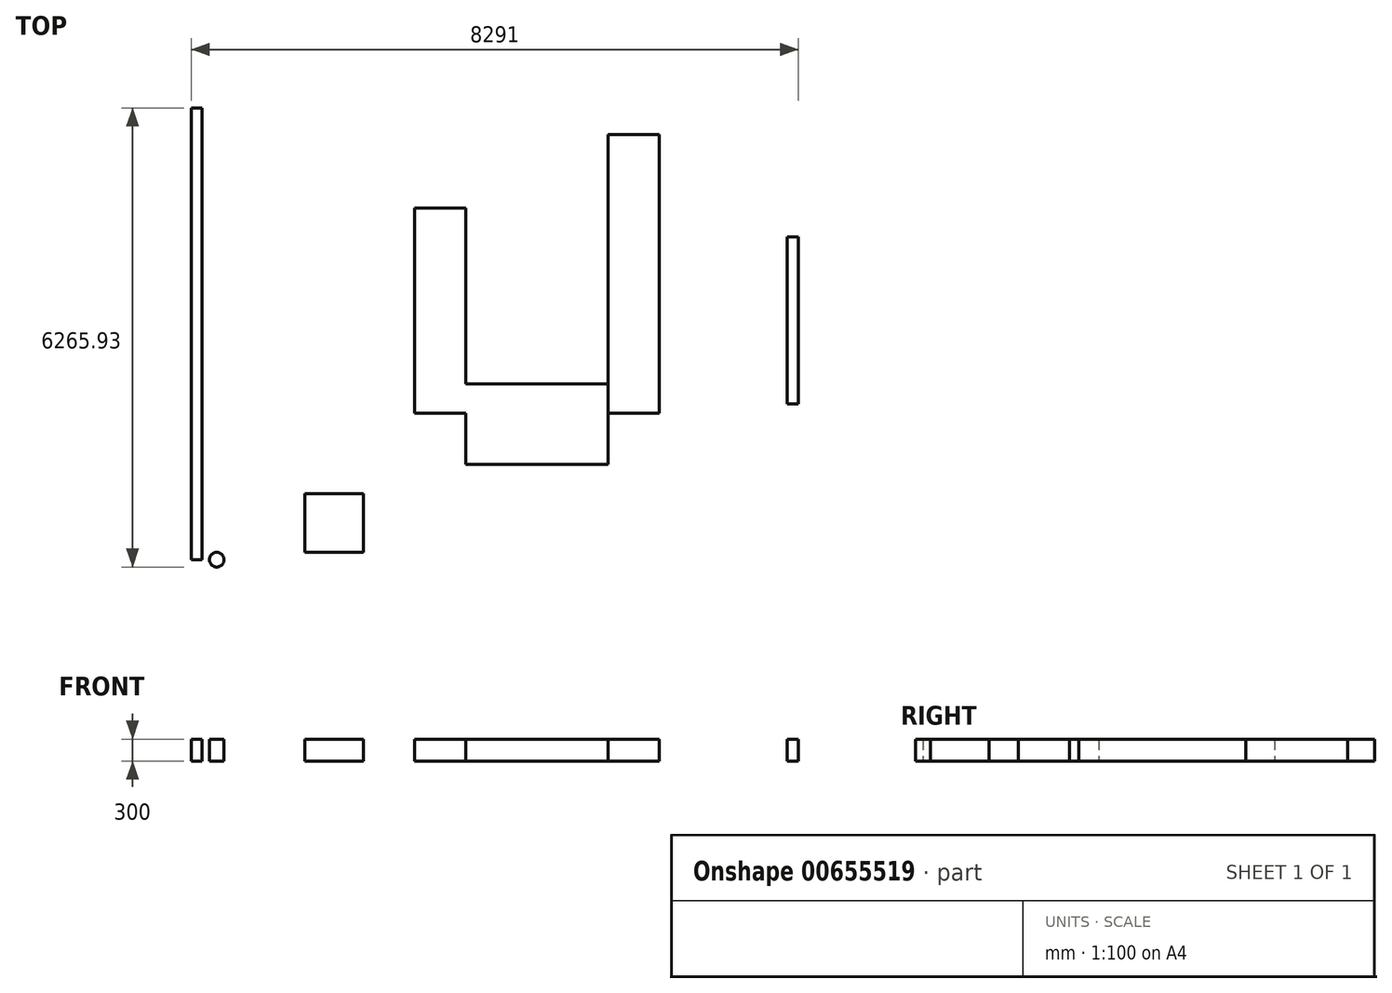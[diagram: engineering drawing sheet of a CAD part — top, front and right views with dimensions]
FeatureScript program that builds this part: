
annotation { "Feature Type Name" : "Feature", "Feature Type Description" : "" }
export const myFeature = defineFeature(function(context is Context, id is Id, definition is map)
    precondition{}
    {
        {
            var Q0;
            Q0=qCreatedBy(makeId("Top.planeOp"),FACE);
            var sketch = newSketch(context, id + "F0", { "sketchPlane" : qUnion([Q0])});
            skLineSegment(sketch, "E0.top", {"start": v(0, 700) * mm, "end": v(-300, 700) * mm, "construction": true});
            skLineSegment(sketch, "E0.left", {"start": v(0, 0) * mm, "end": v(0, 700) * mm, "construction": true});
            skLineSegment(sketch, "E1.bottom", {"start": v(800, -950) * mm, "end": v(2740, -950) * mm});
            skLineSegment(sketch, "E1.top", {"start": v(800, -1350) * mm, "end": v(2740, -1350) * mm});
            skLineSegment(sketch, "E1.left", {"start": v(800, -950) * mm, "end": v(800, -1350) * mm});
            skLineSegment(sketch, "E1.right", {"start": v(2740, -950) * mm, "end": v(2740, -1350) * mm});
            skLineSegment(sketch, "E2", {"start": v(5191, 1057.48) * mm, "end": v(5191, -1222.08) * mm});
            skLineSegment(sketch, "E3.bottom", {"start": v(800, -950) * mm, "end": v(100, -950) * mm});
            skLineSegment(sketch, "E3.top", {"start": v(800, 1450) * mm, "end": v(100, 1450) * mm});
            skLineSegment(sketch, "E3.left", {"start": v(800, -950) * mm, "end": v(800, 1450) * mm});
            skLineSegment(sketch, "E3.right", {"start": v(100, -950) * mm, "end": v(100, 1450) * mm});
            skLineSegment(sketch, "E4", {"start": v(-1400, -3250) * mm, "end": v(-1400, -2450) * mm});
            skLineSegment(sketch, "E5", {"start": v(-1400, -2450) * mm, "end": v(-600, -2450) * mm});
            skLineSegment(sketch, "E6", {"start": v(-600, -2450) * mm, "end": v(-600, -3250) * mm});
            skLineSegment(sketch, "E7", {"start": v(-600, -3250) * mm, "end": v(-1400, -3250) * mm});
            skCircle(sketch, "E8", {"center": v(-2600, -3350) * mm, "radius": 100 * mm});
            skLineSegment(sketch, "E9", {"start": v(5191, 1057.48) * mm, "end": v(5341, 1057.48) * mm});
            skLineSegment(sketch, "E10", {"start": v(5341, 1057.48) * mm, "end": v(5341, -1222.08) * mm});
            skLineSegment(sketch, "E11", {"start": v(5341, -1222.08) * mm, "end": v(5191, -1222.08) * mm});
            skLineSegment(sketch, "E12", {"start": v(100, -950) * mm, "end": v(100, -1350) * mm});
            skLineSegment(sketch, "E13", {"start": v(100, -1350) * mm, "end": v(800, -1350) * mm});
            skLineSegment(sketch, "E14", {"start": v(-2800, -3350) * mm, "end": v(-2800, 2815.93) * mm});
            skLineSegment(sketch, "E15", {"start": v(-2800, 2815.93) * mm, "end": v(-2950, 2815.93) * mm});
            skLineSegment(sketch, "E16", {"start": v(-2950, 2815.93) * mm, "end": v(-2950, -3350) * mm});
            skLineSegment(sketch, "E17", {"start": v(-2950, -3350) * mm, "end": v(-2800, -3350) * mm});
            skLineSegment(sketch, "E18", {"start": v(800, -1350) * mm, "end": v(800, -2050) * mm});
            skLineSegment(sketch, "E19", {"start": v(800, -2050) * mm, "end": v(2740, -2050) * mm});
            skLineSegment(sketch, "E20", {"start": v(2740, -2050) * mm, "end": v(2740, -1350) * mm});
            skLineSegment(sketch, "E21", {"start": v(800, -2050) * mm, "end": v(-600, -2450) * mm, "construction": true});
            skLineSegment(sketch, "E22", {"start": v(800, -1500) * mm, "end": v(2740, -1500) * mm, "construction": true});
            skLineSegment(sketch, "E23", {"start": v(-550, 700) * mm, "end": v(-550, 0) * mm, "construction": true});
            skLineSegment(sketch, "E24", {"start": v(-550, 700) * mm, "end": v(-300, 700) * mm, "construction": true});
            skLineSegment(sketch, "E25", {"start": v(-150, 700) * mm, "end": v(-150, 0) * mm, "construction": true});
            skLineSegment(sketch, "E26", {"start": v(-550, 700) * mm, "end": v(-700, 700) * mm, "construction": true});
            skLineSegment(sketch, "E27", {"start": v(-700, 700) * mm, "end": v(-700, 0) * mm, "construction": true});
            skLineSegment(sketch, "E28", {"start": v(800, -800) * mm, "end": v(2740, -800) * mm, "construction": true});
            skArc(sketch, "E29", {"start": v(0, 0) * mm, "mid": v(234.31, -565.69) * mm, "end": v(800, -800) * mm, "construction": true});
            skArc(sketch, "E30", {"start": v(-150, 0) * mm, "mid": v(128.25, -671.75) * mm, "end": v(800, -950) * mm, "construction": true});
            skArc(sketch, "E31", {"start": v(-550, 0) * mm, "mid": v(-154.6, -954.6) * mm, "end": v(800, -1350) * mm, "construction": true});
            skArc(sketch, "E32", {"start": v(-700, 0) * mm, "mid": v(-260.66, -1060.66) * mm, "end": v(800, -1500) * mm, "construction": true});
            skLineSegment(sketch, "E33", {"start": v(-700, 0) * mm, "end": v(-550, 0) * mm, "construction": true});
            skLineSegment(sketch, "E34", {"start": v(-550, 0) * mm, "end": v(-150, 0) * mm, "construction": true});
            skLineSegment(sketch, "E35", {"start": v(-150, 0) * mm, "end": v(0, 0) * mm, "construction": true});
            skLineSegment(sketch, "E36", {"start": v(-700, 700) * mm, "end": v(-700, 3100) * mm, "construction": true});
            skLineSegment(sketch, "E37", {"start": v(-700, 3100) * mm, "end": v(0, 3100) * mm, "construction": true});
            skLineSegment(sketch, "E38", {"start": v(0, 3100) * mm, "end": v(0, 700) * mm, "construction": true});
            skLineSegment(sketch, "E39.bottom", {"start": v(2741, -1349) * mm, "end": v(3441, -1349) * mm});
            skLineSegment(sketch, "E39.top", {"start": v(2741, 2451) * mm, "end": v(3441, 2451) * mm});
            skLineSegment(sketch, "E39.left", {"start": v(2741, -1349) * mm, "end": v(2741, 2451) * mm});
            skLineSegment(sketch, "E39.right", {"start": v(3441, -1349) * mm, "end": v(3441, 2451) * mm});
            skSolve(sketch);
        }
        {
            var Q0;
            Q0=qSketchRegion(id+"F0",true);
            extrude(context, id + "F1", {"entities" : qUnion([Q0]), "depth" : 300 * mm, "offsetDistance" : 25 * mm});
        }
    });
